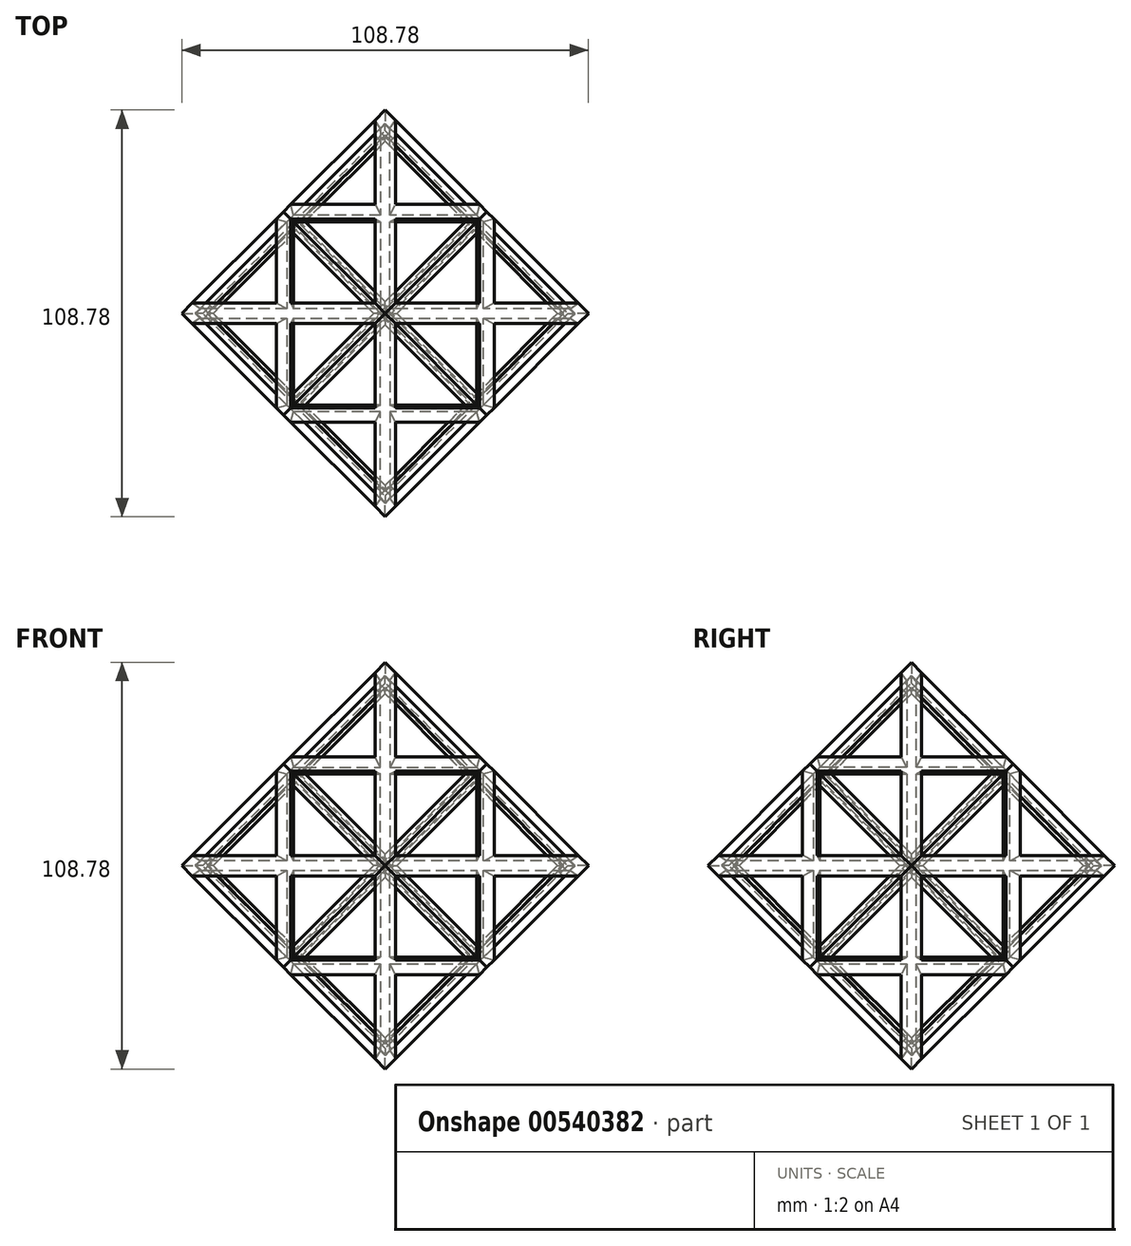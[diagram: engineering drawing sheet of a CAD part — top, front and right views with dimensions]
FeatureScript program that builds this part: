
annotation { "Feature Type Name" : "Feature", "Feature Type Description" : "" }
export const myFeature = defineFeature(function(context is Context, id is Id, definition is map)
    precondition{}
    {
        {
            var Q0;
            Q0=qCreatedBy(makeId("Right.planeOp"),FACE);
            cPlane(context, id + "F0", {"entities" : qUnion([Q0]), "cplaneType" : CPlaneType.OFFSET, "offset" : 25.4 * mm, "width" : 152.4 * mm, "height" : 152.4 * mm});
        }
        {
            var Q0;
            Q0=qCreatedBy(makeId("Right.planeOp"),FACE);
            cPlane(context, id + "F1", {"entities" : qUnion([Q0]), "cplaneType" : CPlaneType.OFFSET, "offset" : 25.4 * mm, "oppositeDirection" : true, "width" : 152.4 * mm, "height" : 152.4 * mm});
        }
        {
            var Q0;
            Q0=qCreatedBy(makeId("Right.planeOp"),FACE);
            var sketch = newSketch(context, id + "F2", { "sketchPlane" : qUnion([Q0])});
            skPoint(sketch, "E0", {"position": v(0, 50.8) * mm});
            skPoint(sketch, "E1", {"position": v(-50.8, 0) * mm});
            skPoint(sketch, "E2", {"position": v(0, -50.8) * mm});
            skPoint(sketch, "E3", {"position": v(50.8, 0) * mm});
            skSolve(sketch);
        }
        {
            var Q0;
            Q0=qCreatedBy(id+"F0.planeOp",FACE);
            var sketch = newSketch(context, id + "F3", { "sketchPlane" : qUnion([Q0])});
            skPoint(sketch, "E4", {"position": v(25.4, 25.4) * mm});
            skPoint(sketch, "E5", {"position": v(25.4, -25.4) * mm});
            skPoint(sketch, "E6", {"position": v(-25.4, -25.4) * mm});
            skPoint(sketch, "E7", {"position": v(-25.4, 25.4) * mm});
            skSolve(sketch);
        }
        {
            var Q0;
            Q0=qCreatedBy(id+"F1.planeOp",FACE);
            var sketch = newSketch(context, id + "F4", { "sketchPlane" : qUnion([Q0])});
            skPoint(sketch, "E8", {"position": v(-25.4, 25.4) * mm});
            skPoint(sketch, "E9", {"position": v(25.4, 25.4) * mm});
            skPoint(sketch, "E10", {"position": v(25.4, -25.4) * mm});
            skPoint(sketch, "E11", {"position": v(-25.4, -25.4) * mm});
            skSolve(sketch);
        }
        {
            var Q0;
            Q0=sQuery(id+"F4.wireOp",VERTEX,"E8");
            var Q1;
            Q1=sQuery(id+"F2.wireOp",VERTEX,"E0");
            var Q2;
            Q2=sQuery(id+"F3.wireOp",VERTEX,"E7");
            cPlane(context, id + "F5", {"entities" : qUnion([Q0, Q1, Q2]), "cplaneType" : CPlaneType.THREE_POINT, "offset" : 25.4 * mm, "width" : 152.4 * mm, "height" : 152.4 * mm});
        }
        {
            var Q0;
            Q0=qCreatedBy(id+"F5.planeOp",FACE);
            var sketch = newSketch(context, id + "F6", { "sketchPlane" : qUnion([Q0])});
            skLineSegment(sketch, "E12", {"start": v(-25.4, 0) * mm, "end": v(0, 35.92) * mm});
            skLineSegment(sketch, "E13", {"start": v(0, 35.92) * mm, "end": v(25.4, 0) * mm});
            skLineSegment(sketch, "E14", {"start": v(25.4, 0) * mm, "end": v(0, -35.92) * mm});
            skLineSegment(sketch, "E15", {"start": v(0, -35.92) * mm, "end": v(-25.4, 0) * mm});
            skLineSegment(sketch, "E16.0", {"start": v(0, 31.52) * mm, "end": v(22.29, 0) * mm});
            skLineSegment(sketch, "E16.1", {"start": v(-22.29, 0) * mm, "end": v(0, 31.52) * mm});
            skLineSegment(sketch, "E16.2", {"start": v(0, -31.52) * mm, "end": v(-22.29, 0) * mm});
            skLineSegment(sketch, "E16.3", {"start": v(22.29, 0) * mm, "end": v(0, -31.52) * mm});
            skSolve(sketch);
        }
        {
            var Q0;
            Q0=makeQuery(id+"F6.imprint","IMPRINT",FACE,{"disambiguationData":[TD([[makeQuery(id+"F6.imprint","IMPRINT",EDGE,{"derivedFrom":sQuery(id+"F6.wireOp",EDGE,"E12")}),-1.0]])]});
            extrude(context, id + "F7", {"entities" : qUnion([Q0]), "oppositeDirection" : true, "depth" : 2.54 * mm, "hasDraft" : true, "draftAngle" : 3 * degree, "draftPullDirection" : true});
        }
        {
            var Q0;
            Q0=makeQuery(id+"F7.opExtrude","CAP_FACE",FACE,{"disambiguationData":[OSD([sQuery(id+"F6.wireOp",EDGE,"E12"),sQuery(id+"F6.wireOp",EDGE,"E13"),sQuery(id+"F6.wireOp",EDGE,"E14"),sQuery(id+"F6.wireOp",EDGE,"E15"),sQuery(id+"F6.wireOp",EDGE,"E16.0"),sQuery(id+"F6.wireOp",EDGE,"E16.1"),sQuery(id+"F6.wireOp",EDGE,"E16.2"),sQuery(id+"F6.wireOp",EDGE,"E16.3")])],"isStart":true});
            var sketch = newSketch(context, id + "F8", { "sketchPlane" : qUnion([Q0])});
            skLineSegment(sketch, "E17", {"start": v(-25.4, 0) * mm, "end": v(-24.5, 1.27) * mm});
            skLineSegment(sketch, "E18", {"start": v(-24.5, 1.27) * mm, "end": v(24.5, 1.27) * mm});
            skLineSegment(sketch, "E19", {"start": v(24.5, 1.27) * mm, "end": v(25.4, 0) * mm});
            skLineSegment(sketch, "E20", {"start": v(25.4, 0) * mm, "end": v(24.5, -1.27) * mm});
            skLineSegment(sketch, "E21", {"start": v(24.5, -1.27) * mm, "end": v(-24.5, -1.27) * mm});
            skLineSegment(sketch, "E22", {"start": v(-24.5, -1.27) * mm, "end": v(-25.4, 0) * mm});
            skSolve(sketch);
        }
        {
            var Q0;
            {var subQ0=sQuery(id+"F6.wireOp",EDGE,"E16.2");var subQ2=sQuery(id+"F6.wireOp",EDGE,"E15");var subQ3=sQuery(id+"F6.wireOp",EDGE,"E16.3");var subQ5=sQuery(id+"F6.wireOp",EDGE,"E14");Q0=makeQuery(id+"F10.boolean.opBoolean","SPLIT",FACE,{"disambiguationData":[TD([makeQuery(id+"F7.opExtrude","SWEPT_FACE",FACE,{"disambiguationData":[OSD([subQ5])]})])],"derivedFrom":makeQuery(id+"F7.opExtrude","CAP_FACE",FACE,{"disambiguationData":[OSD([sQuery(id+"F6.wireOp",EDGE,"E12"),sQuery(id+"F6.wireOp",EDGE,"E13"),subQ5,subQ2,sQuery(id+"F6.wireOp",EDGE,"E16.0"),sQuery(id+"F6.wireOp",EDGE,"E16.1"),subQ0,subQ3])],"isStart":true})});}
            var sketch = newSketch(context, id + "F9", { "sketchPlane" : qUnion([Q0])});
            skLineSegment(sketch, "E23", {"start": v(0, -35.92) * mm, "end": v(1.27, -34.12) * mm});
            skLineSegment(sketch, "E24", {"start": v(1.27, -34.12) * mm, "end": v(1.27, 34.12) * mm});
            skLineSegment(sketch, "E25", {"start": v(1.27, 34.12) * mm, "end": v(0, 35.92) * mm});
            skLineSegment(sketch, "E26", {"start": v(0, 35.92) * mm, "end": v(-1.27, 34.12) * mm});
            skLineSegment(sketch, "E27", {"start": v(-1.27, 34.12) * mm, "end": v(-1.27, -34.12) * mm});
            skLineSegment(sketch, "E28", {"start": v(-1.27, -34.12) * mm, "end": v(0, -35.92) * mm});
            skSolve(sketch);
        }
        {
            var Q0;
            Q0 = qSketchRegion(id + "F8", true);
            extrude(context, id + "F10", {"entities" : qUnion([Q0]), "operationType" : NewBodyOperationType.ADD, "depth" : 2.54 * mm, "offsetDistance" : 25.4 * mm, "hasDraft" : true, "draftAngle" : 30 * degree});
        }
        {
            var Q0;
            Q0 = qSketchRegion(id + "F9", true);
            extrude(context, id + "F11", {"entities" : qUnion([Q0]), "operationType" : NewBodyOperationType.ADD, "depth" : 2.54 * mm, "offsetDistance" : 25.4 * mm, "hasDraft" : true, "draftAngle" : 30 * degree});
        }
        {
            var Q0;
            Q0=qCreatedBy(makeId("Front.planeOp"),FACE);
            var sketch = newSketch(context, id + "F12", { "sketchPlane" : qUnion([Q0])});
            skLineSegment(sketch, "E29", {"start": v(0, 50.8) * mm, "end": v(0, -50.8) * mm, "construction": true});
            skSolve(sketch);
        }
        {
            var Q0;
            Q0=makeQuery(id+"F7.opExtrude","SWEPT_BODY",BODY,{"disambiguationData":[OSD([sQuery(id+"F6.wireOp",EDGE,"E12"),sQuery(id+"F6.wireOp",EDGE,"E13"),sQuery(id+"F6.wireOp",EDGE,"E14"),sQuery(id+"F6.wireOp",EDGE,"E15")])]});
            var Q1;
            Q1=sQuery(id+"F12.wireOp",EDGE,"E29");
            circularPattern(context, id + "F13", {"entities" : qUnion([Q0]), "axis" : qUnion([Q1]), "angle" : 360 * degree, "instanceCount" : 4, "equalSpace" : true});
        }
        {
            var Q0;
            Q0=qCreatedBy(makeId("Right.planeOp"),FACE);
            var sketch = newSketch(context, id + "F14", { "sketchPlane" : qUnion([Q0])});
            skLineSegment(sketch, "E30", {"start": v(50.8, 0) * mm, "end": v(-50.8, 0) * mm, "construction": true});
            skSolve(sketch);
        }
        {
            var Q0;
            Q0=makeQuery(id+"F13.opPattern","COPY",BODY,{"derivedFrom":makeQuery(id+"F7.opExtrude","SWEPT_BODY",BODY,{"disambiguationData":[OSD([sQuery(id+"F6.wireOp",EDGE,"E12"),sQuery(id+"F6.wireOp",EDGE,"E13"),sQuery(id+"F6.wireOp",EDGE,"E14"),sQuery(id+"F6.wireOp",EDGE,"E15")])]}),"instanceName":"2"});
            var Q1;
            Q1=sQuery(id+"F14.wireOp",EDGE,"E30");
            circularPattern(context, id + "F15", {"entities" : qUnion([Q0]), "axis" : qUnion([Q1]), "angle" : 360 * degree, "instanceCount" : 4, "equalSpace" : true});
        }
        {
            var Q0;
            Q0=makeQuery(id+"F7.opExtrude","SWEPT_BODY",BODY,{"disambiguationData":[OSD([sQuery(id+"F6.wireOp",EDGE,"E12"),sQuery(id+"F6.wireOp",EDGE,"E13"),sQuery(id+"F6.wireOp",EDGE,"E14"),sQuery(id+"F6.wireOp",EDGE,"E15")])]});
            var Q1;
            Q1=sQuery(id+"F14.wireOp",EDGE,"E30");
            circularPattern(context, id + "F16", {"entities" : qUnion([Q0]), "axis" : qUnion([Q1]), "angle" : 360 * degree, "instanceCount" : 4, "equalSpace" : true});
        }
        {
            var Q0;
            Q0=qCreatedBy(makeId("Front.planeOp"),FACE);
            var sketch = newSketch(context, id + "F17", { "sketchPlane" : qUnion([Q0])});
            skLineSegment(sketch, "E31", {"start": v(0, 50.8) * mm, "end": v(0, -50.8) * mm, "construction": true});
            skSolve(sketch);
        }
        {
            var Q0;
            Q0=makeQuery(id+"F15.opPattern","COPY",BODY,{"derivedFrom":makeQuery(id+"F13.opPattern","COPY",BODY,{"derivedFrom":makeQuery(id+"F7.opExtrude","SWEPT_BODY",BODY,{"disambiguationData":[OSD([sQuery(id+"F6.wireOp",EDGE,"E12"),sQuery(id+"F6.wireOp",EDGE,"E13"),sQuery(id+"F6.wireOp",EDGE,"E14"),sQuery(id+"F6.wireOp",EDGE,"E15")])]}),"instanceName":"2"}),"instanceName":"2"});
            var Q1;
            Q1=sQuery(id+"F17.wireOp",EDGE,"E31");
            circularPattern(context, id + "F18", {"entities" : qUnion([Q0]), "axis" : qUnion([Q1]), "angle" : 90 * degree, "instanceCount" : 2, "equalSpace" : true});
        }
        {
            var Q0;
            Q0=makeQuery(id+"F15.opPattern","COPY",BODY,{"derivedFrom":makeQuery(id+"F13.opPattern","COPY",BODY,{"derivedFrom":makeQuery(id+"F7.opExtrude","SWEPT_BODY",BODY,{"disambiguationData":[OSD([sQuery(id+"F6.wireOp",EDGE,"E12"),sQuery(id+"F6.wireOp",EDGE,"E13"),sQuery(id+"F6.wireOp",EDGE,"E14"),sQuery(id+"F6.wireOp",EDGE,"E15")])]}),"instanceName":"2"}),"instanceName":"2"});
            var Q1;
            Q1=sQuery(id+"F17.wireOp",EDGE,"E31");
            circularPattern(context, id + "F19", {"entities" : qUnion([Q0]), "axis" : qUnion([Q1]), "angle" : 90 * degree, "instanceCount" : 2, "oppositeDirection" : true, "equalSpace" : true});
        }
    });
